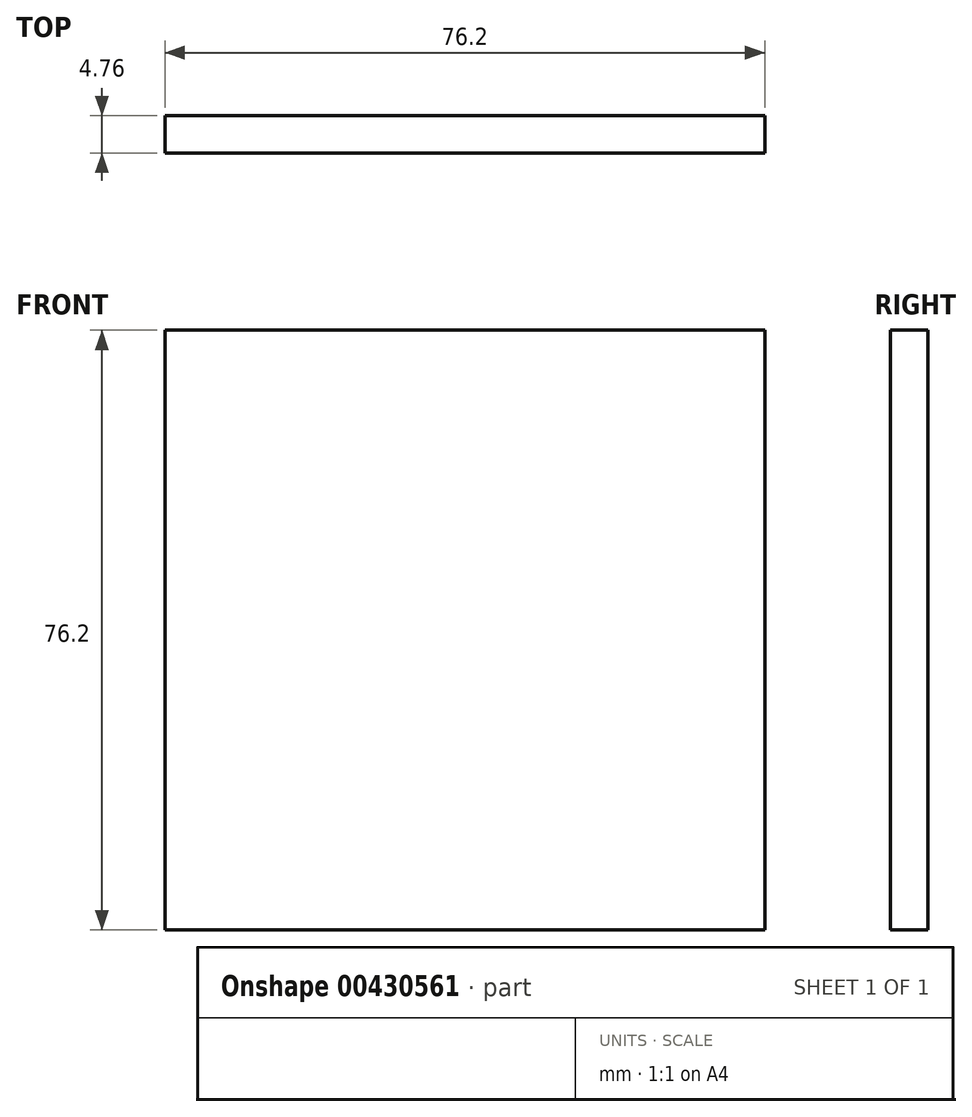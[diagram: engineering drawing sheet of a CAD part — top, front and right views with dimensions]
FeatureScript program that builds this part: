
annotation { "Feature Type Name" : "Feature", "Feature Type Description" : "" }
export const myFeature = defineFeature(function(context is Context, id is Id, definition is map)
    precondition{}
    {
        {
            var Q0;
            Q0=qCreatedBy(makeId("Front.planeOp"),FACE);
            var sketch = newSketch(context, id + "F0", { "sketchPlane" : qUnion([Q0])});
            skLineSegment(sketch, "E0.bottom", {"start": v(-20, 48.85) * mm, "end": v(56.2, 48.85) * mm});
            skLineSegment(sketch, "E0.top", {"start": v(-20, -27.35) * mm, "end": v(56.2, -27.35) * mm});
            skLineSegment(sketch, "E0.left", {"start": v(-20, 48.85) * mm, "end": v(-20, -27.35) * mm});
            skLineSegment(sketch, "E0.right", {"start": v(56.2, 48.85) * mm, "end": v(56.2, -27.35) * mm});
            skSolve(sketch);
        }
        {
            var Q0;
            Q0=makeQuery(id+"F0.imprint","IMPRINT",FACE,{"disambiguationData":[TD([[makeQuery(id+"F0.imprint","IMPRINT",EDGE,{"derivedFrom":sQuery(id+"F0.wireOp",EDGE,"E0.bottom")}),-1.0]])]});
            extrude(context, id + "F1", {"entities" : qUnion([Q0]), "depth" : 4.76 * mm});
        }
    });
